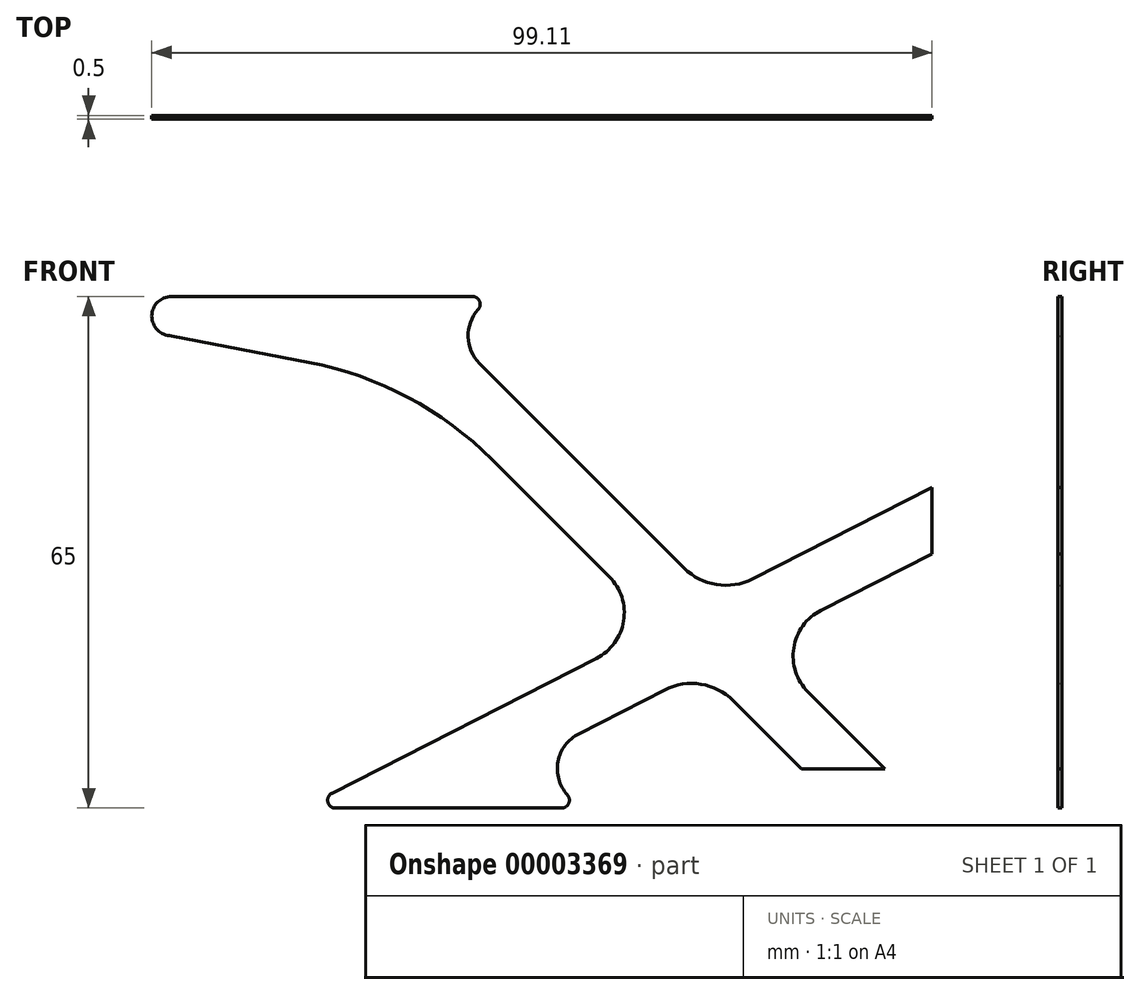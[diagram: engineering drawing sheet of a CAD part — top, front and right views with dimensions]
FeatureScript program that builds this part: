
annotation { "Feature Type Name" : "Feature", "Feature Type Description" : "" }
export const myFeature = defineFeature(function(context is Context, id is Id, definition is map)
    precondition{}
    {
        {
            var Q0;
            Q0=qCreatedBy(makeId("Front.planeOp"),FACE);
            var sketch = newSketch(context, id + "F0", { "sketchPlane" : qUnion([Q0])});
            skLineSegment(sketch, "E0", {"start": v(10.6, 0) * mm, "end": v(0.86, 9.74) * mm});
            skLineSegment(sketch, "E1", {"start": v(0, 0) * mm, "end": v(-8.64, 8.64) * mm});
            skLineSegment(sketch, "E2", {"start": v(16.6, 35.73) * mm, "end": v(-6.18, 24.12) * mm});
            skLineSegment(sketch, "E3", {"start": v(-28.26, 4.46) * mm, "end": v(-17.34, 10.02) * mm});
            skLineSegment(sketch, "E4", {"start": v(10.6, 0) * mm, "end": v(0, 0) * mm});
            skLineSegment(sketch, "E5.trimOffspring", {"start": v(-24.4, 24.4) * mm, "end": v(-39.26, 39.26) * mm});
            skArc(sketch, "E6.filletArc", {"start": v(-26.04, 14) * mm, "mid": v(-22.57, 18.78) * mm, "end": v(-24.4, 24.4) * mm});
            skArc(sketch, "E7.filletArc", {"start": v(-8.64, 8.64) * mm, "mid": v(-12.77, 10.74) * mm, "end": v(-17.34, 10.02) * mm});
            skLineSegment(sketch, "E8", {"start": v(-80, 55) * mm, "end": v(-62.53, 51.62) * mm});
            skArc(sketch, "E9.filletArc", {"start": v(-39.26, 39.26) * mm, "mid": v(-49.97, 47.18) * mm, "end": v(-62.53, 51.62) * mm});
            skLineSegment(sketch, "E10", {"start": v(16.6, 27.31) * mm, "end": v(16.6, 35.73) * mm});
            skLineSegment(sketch, "E11.trimOffspring", {"start": v(-14.9, 25.5) * mm, "end": v(-40.86, 51.46) * mm});
            skLineSegment(sketch, "E12.trimOffspring", {"start": v(-26.04, 14) * mm, "end": v(-59.62, -3.1) * mm});
            skLineSegment(sketch, "E13.trimOffspring", {"start": v(2.5, 20.13) * mm, "end": v(16.6, 27.31) * mm});
            skArc(sketch, "E14.filletArc", {"start": v(-14.9, 25.5) * mm, "mid": v(-10.76, 23.4) * mm, "end": v(-6.18, 24.12) * mm});
            skArc(sketch, "E15.filletArc", {"start": v(2.5, 20.13) * mm, "mid": v(-0.96, 15.36) * mm, "end": v(0.86, 9.74) * mm});
            skArc(sketch, "E16.filletArc", {"start": v(-28.26, 4.46) * mm, "mid": v(-30.9, 0.92) * mm, "end": v(-29.71, -3.33) * mm});
            skLineSegment(sketch, "E17", {"start": v(-59.17, -5) * mm, "end": v(-30.46, -5) * mm});
            skLineSegment(sketch, "E18.0", {"start": v(-41.8, 60) * mm, "end": v(-80, 60) * mm});
            skArc(sketch, "E19.filletArc", {"start": v(-41.05, 58.33) * mm, "mid": v(-42.32, 54.86) * mm, "end": v(-40.86, 51.46) * mm});
            skArc(sketch, "E20.filletArc", {"start": v(-41.05, 58.33) * mm, "mid": v(-40.88, 59.4) * mm, "end": v(-41.8, 60) * mm});
            skArc(sketch, "E21.filletArc", {"start": v(-30.46, -5) * mm, "mid": v(-29.55, -4.4) * mm, "end": v(-29.71, -3.33) * mm});
            skArc(sketch, "E22.filletArc", {"start": v(-59.62, -3.1) * mm, "mid": v(-60.14, -4.23) * mm, "end": v(-59.17, -5) * mm});
            skArc(sketch, "E23", {"start": v(-80, 55) * mm, "mid": v(-82.5, 57.5) * mm, "end": v(-80, 60) * mm});
            skSolve(sketch);
        }
        {
            var Q0;
            Q0=makeQuery(id+"F0.imprint","IMPRINT",FACE,{"disambiguationData":[TD([[makeQuery(id+"F0.imprint","IMPRINT",EDGE,{"derivedFrom":sQuery(id+"F0.wireOp",EDGE,"E0")}),1.0]])]});
            extrude(context, id + "F1", {"entities" : qUnion([Q0]), "depth" : .5 * mm});
        }
    });
